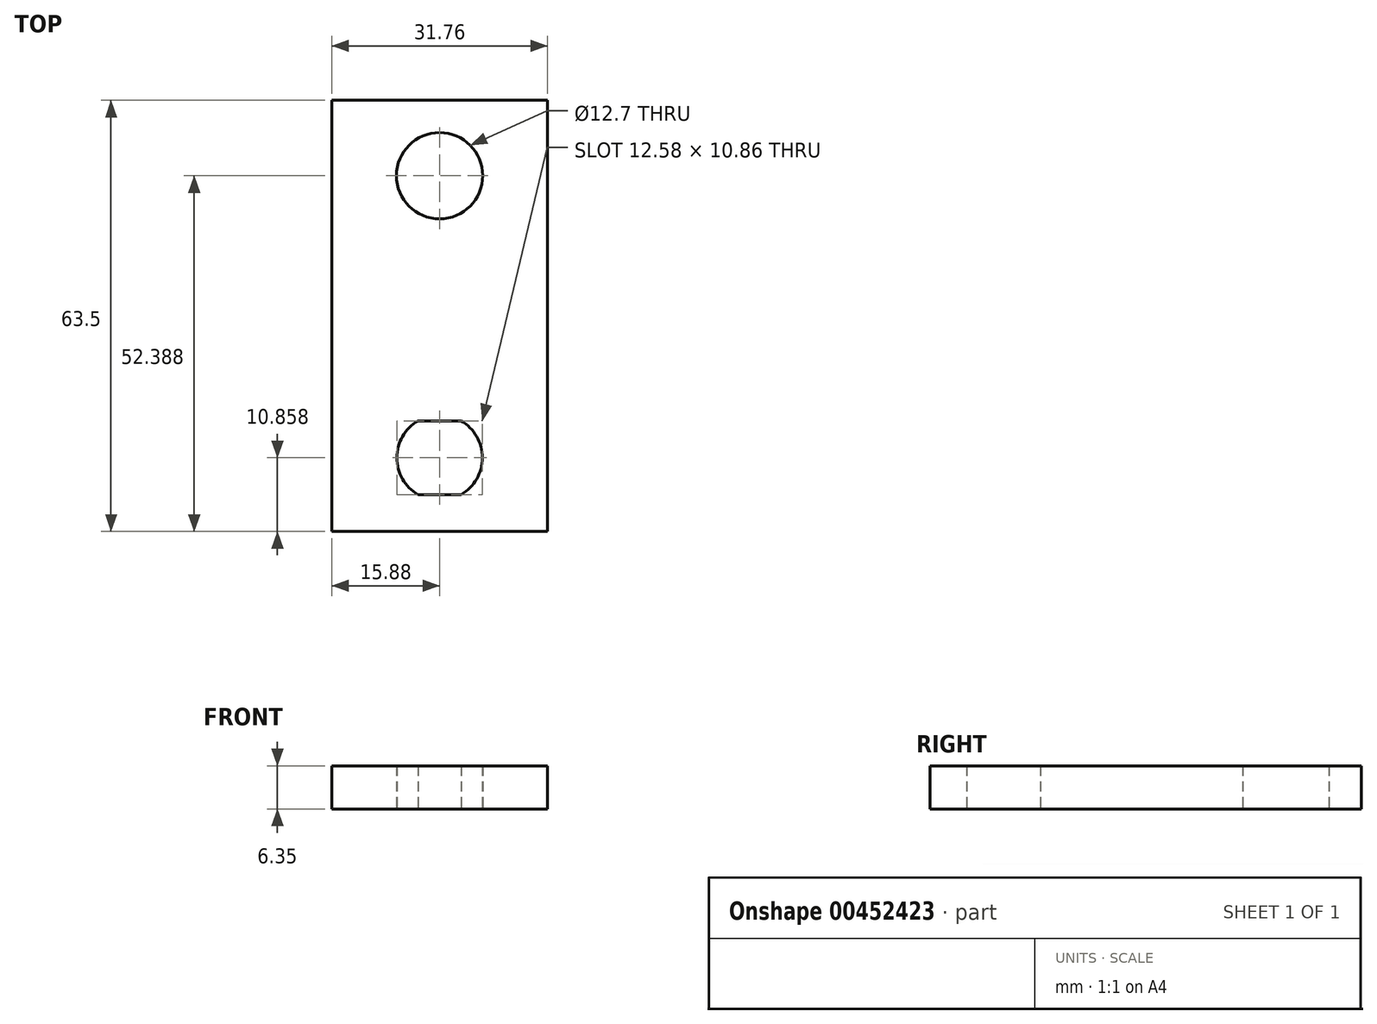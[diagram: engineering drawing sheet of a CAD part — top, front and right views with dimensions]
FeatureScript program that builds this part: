
annotation { "Feature Type Name" : "Feature", "Feature Type Description" : "" }
export const myFeature = defineFeature(function(context is Context, id is Id, definition is map)
    precondition{}
    {
        {
            var Q0;
            Q0=qCreatedBy(makeId("Top.planeOp"),FACE);
            var sketch = newSketch(context, id + "F0", { "sketchPlane" : qUnion([Q0])});
            skLineSegment(sketch, "E0.bottom", {"start": v(15.88, -31.75) * mm, "end": v(-15.88, -31.75) * mm});
            skLineSegment(sketch, "E0.top", {"start": v(15.88, 31.75) * mm, "end": v(-15.88, 31.75) * mm});
            skLineSegment(sketch, "E0.left", {"start": v(15.87, -31.75) * mm, "end": v(15.88, 31.75) * mm});
            skLineSegment(sketch, "E0.right", {"start": v(-15.88, -31.75) * mm, "end": v(-15.88, 31.75) * mm});
            skPoint(sketch, "E0.middle", {"position": v(0, 0) * mm});
            skCircle(sketch, "E1", {"center": v(0, 20.64) * mm, "radius": 6.35 * mm});
            skLineSegment(sketch, "E2.bottom", {"start": v(3.18, -26.32) * mm, "end": v(-3.17, -26.32) * mm});
            skLineSegment(sketch, "E2.top", {"start": v(3.17, -15.46) * mm, "end": v(-3.18, -15.46) * mm});
            skPoint(sketch, "E2.middle", {"position": v(0, -20.9) * mm});
            skArc(sketch, "E3", {"start": v(3.18, -15.46) * mm, "mid": v(6.29, -20.9) * mm, "end": v(3.18, -26.32) * mm});
            skArc(sketch, "E4", {"start": v(-3.18, -15.46) * mm, "mid": v(-6.29, -20.9) * mm, "end": v(-3.17, -26.32) * mm});
            skSolve(sketch);
        }
        {
            var Q0;
            Q0=makeQuery(id+"F0.imprint","IMPRINT",FACE,{"disambiguationData":[TD([[makeQuery(id+"F0.imprint","IMPRINT",EDGE,{"derivedFrom":sQuery(id+"F0.wireOp",EDGE,"E0.bottom")}),-1.0]])]});
            extrude(context, id + "F1", {"entities" : qUnion([Q0]), "depth" : 6.35 * mm});
        }
    });
